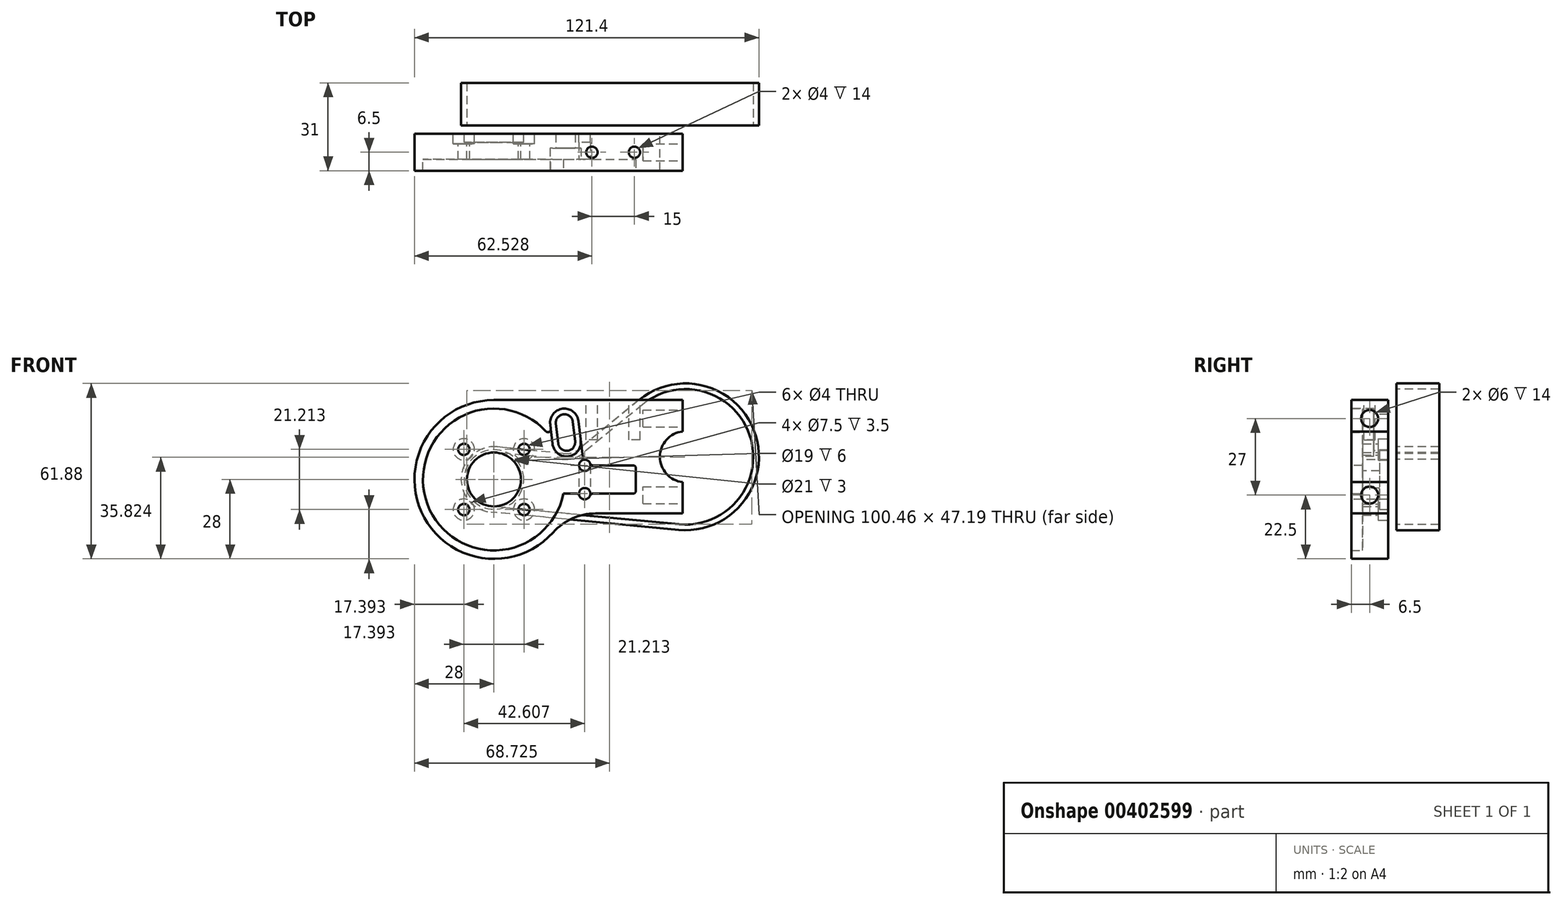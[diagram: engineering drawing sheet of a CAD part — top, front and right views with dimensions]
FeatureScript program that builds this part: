
annotation { "Feature Type Name" : "Feature", "Feature Type Description" : "" }
export const myFeature = defineFeature(function(context is Context, id is Id, definition is map)
    precondition{}
    {
        {
            var Q0;
            Q0=qCreatedBy(makeId("Front.planeOp"),FACE);
            var sketch = newSketch(context, id + "F0", { "sketchPlane" : qUnion([Q0])});
            skArc(sketch, "E0", {"start": v(66.53, 16.94) * mm, "mid": v(58.53, 8) * mm, "end": v(66.53, -0.94) * mm});
            skLineSegment(sketch, "E1", {"start": v(66.53, 16.94) * mm, "end": v(66.53, 28) * mm});
            skLineSegment(sketch, "E2", {"start": v(66.53, -0.94) * mm, "end": v(66.53, -12) * mm});
            skLineSegment(sketch, "E3", {"start": v(66.53, 16.94) * mm, "end": v(66.53, 8) * mm, "construction": true});
            skLineSegment(sketch, "E4", {"start": v(66.53, 8) * mm, "end": v(66.53, -0.94) * mm, "construction": true});
            skArc(sketch, "E5", {"start": v(0, 28) * mm, "mid": v(-25.56, -11.43) * mm, "end": v(20.87, -18.67) * mm});
            skCircle(sketch, "E6", {"center": v(0, 0) * mm, "radius": 11 * mm, "construction": true});
            skLineSegment(sketch, "E7", {"start": v(0, 0) * mm, "end": v(10.6, 10.6) * mm, "construction": true});
            skLineSegment(sketch, "E8", {"start": v(0, 0) * mm, "end": v(-10.6, -10.6) * mm, "construction": true});
            skLineSegment(sketch, "E9", {"start": v(0, 0) * mm, "end": v(10.6, -10.6) * mm, "construction": true});
            skLineSegment(sketch, "E10", {"start": v(0, 0) * mm, "end": v(-10.6, 10.6) * mm, "construction": true});
            skCircle(sketch, "E11", {"center": v(10.6, -10.6) * mm, "radius": 2 * mm});
            skCircle(sketch, "E12", {"center": v(-10.6, -10.6) * mm, "radius": 2 * mm});
            skCircle(sketch, "E13", {"center": v(-10.6, 10.6) * mm, "radius": 2 * mm});
            skCircle(sketch, "E14", {"center": v(10.6, 10.6) * mm, "radius": 2 * mm});
            skLineSegment(sketch, "E15", {"start": v(66.53, 28) * mm, "end": v(0, 28) * mm});
            skLineSegment(sketch, "E16", {"start": v(66.53, -12) * mm, "end": v(35.78, -12) * mm});
            skPoint(sketch, "E17.visualSharp", {"position": v(25.3, -12) * mm});
            skArc(sketch, "E17.filletArc", {"start": v(35.78, -12) * mm, "mid": v(27.61, -13.74) * mm, "end": v(20.87, -18.67) * mm});
            skPoint(sketch, "E18.visualSharp", {"position": v(0, 28) * mm});
            skCircle(sketch, "E19", {"center": v(0, 0) * mm, "radius": 9.55 * mm, "construction": true});
            skLineSegment(sketch, "E20.trimOffspring", {"start": v(58.53, 8) * mm, "end": v(67.53, 8) * mm, "construction": true});
            skPoint(sketch, "E21.trimOffspring.start.orphan", {"position": v(44, -40.8) * mm});
            skLineSegment(sketch, "E22", {"start": v(0, 0) * mm, "end": v(0, 8) * mm, "construction": true});
            skLineSegment(sketch, "E23", {"start": v(0, 8) * mm, "end": v(58.53, 8) * mm, "construction": true});
            skPoint(sketch, "E24.0.midPoint", {"position": v(25.1, 23.83) * mm});
            skCircle(sketch, "E25", {"center": v(0, 0) * mm, "radius": 9 * mm});
            skArc(sketch, "E26", {"start": v(0, 28) * mm, "mid": v(25.56, 11.43) * mm, "end": v(20.87, -18.67) * mm, "construction": true});
            skCircle(sketch, "E27", {"center": v(0, 0) * mm, "radius": 22 * mm, "construction": true});
            skCircle(sketch, "E28", {"center": v(0, 0) * mm, "radius": 25 * mm, "construction": true});
            skCircle(sketch, "E29", {"center": v(67.53, 8) * mm, "radius": 28.65 * mm, "construction": true});
            skCircle(sketch, "E30", {"center": v(67.53, 8) * mm, "radius": 23.88 * mm, "construction": true});
            skPoint(sketch, "E31.orphan", {"position": v(24.2, 21.89) * mm});
            skPoint(sketch, "E24.1.start.orphan", {"position": v(26, 25.77) * mm});
            skPoint(sketch, "E32.start.orphan", {"position": v(29.02, 8) * mm});
            skSolve(sketch);
        }
        {
            var Q0;
            Q0=makeQuery(id+"F0.imprint","IMPRINT",FACE,{"disambiguationData":[TD([[makeQuery(id+"F0.imprint","IMPRINT",EDGE,{"derivedFrom":sQuery(id+"F0.wireOp",EDGE,"E0")}),-1.0]])]});
            extrude(context, id + "F1", {"entities" : qUnion([Q0]), "depth" : 9 * mm});
        }
        {
            var Q0;
            Q0=makeQuery(id+"F1.opExtrude","CAP_FACE",FACE,{"disambiguationData":[OSD([sQuery(id+"F0.wireOp",EDGE,"E0"),sQuery(id+"F0.wireOp",EDGE,"E1"),sQuery(id+"F0.wireOp",EDGE,"E2"),sQuery(id+"F0.wireOp",EDGE,"E5"),sQuery(id+"F0.wireOp",EDGE,"E11"),sQuery(id+"F0.wireOp",EDGE,"E12"),sQuery(id+"F0.wireOp",EDGE,"E13"),sQuery(id+"F0.wireOp",EDGE,"E14"),sQuery(id+"F0.wireOp",EDGE,"E15"),sQuery(id+"F0.wireOp",EDGE,"E16"),sQuery(id+"F0.wireOp",EDGE,"E17.filletArc"),sQuery(id+"F0.wireOp",EDGE,"E25")])],"isStart":true});
            var sketch = newSketch(context, id + "F2", { "sketchPlane" : qUnion([Q0])});
            skCircle(sketch, "E33", {"center": v(0, 0) * mm, "radius": 9.5 * mm});
            skSolve(sketch);
        }
        {
            var Q0;
            Q0 = qSketchRegion(id + "F2", true);
            extrude(context, id + "F3", {"entities" : qUnion([Q0]), "operationType" : NewBodyOperationType.REMOVE, "oppositeDirection" : true, "depth" : 9 * mm});
        }
        {
            var Q0;
            Q0=makeQuery(id+"F1.opExtrude","CAP_FACE",FACE,{"disambiguationData":[OSD([sQuery(id+"F0.wireOp",EDGE,"E0"),sQuery(id+"F0.wireOp",EDGE,"E1"),sQuery(id+"F0.wireOp",EDGE,"E2"),sQuery(id+"F0.wireOp",EDGE,"E5"),sQuery(id+"F0.wireOp",EDGE,"E11"),sQuery(id+"F0.wireOp",EDGE,"E12"),sQuery(id+"F0.wireOp",EDGE,"E13"),sQuery(id+"F0.wireOp",EDGE,"E14"),sQuery(id+"F0.wireOp",EDGE,"E15"),sQuery(id+"F0.wireOp",EDGE,"E16"),sQuery(id+"F0.wireOp",EDGE,"E17.filletArc"),sQuery(id+"F0.wireOp",EDGE,"E25")])],"isStart":false});
            var sketch = newSketch(context, id + "F4", { "sketchPlane" : qUnion([Q0])});
            skArc(sketch, "E34.0", {"start": v(0, 28) * mm, "mid": v(-25.56, -11.43) * mm, "end": v(20.87, -18.67) * mm});
            skLineSegment(sketch, "E35.0", {"start": v(66.53, -12) * mm, "end": v(35.78, -12) * mm});
            skArc(sketch, "E36.0", {"start": v(35.78, -12) * mm, "mid": v(27.61, -13.74) * mm, "end": v(20.87, -18.67) * mm});
            skLineSegment(sketch, "E37.0", {"start": v(66.53, 28) * mm, "end": v(0, 28) * mm});
            skLineSegment(sketch, "E38.0", {"start": v(66.53, -0.94) * mm, "end": v(66.53, -12) * mm});
            skArc(sketch, "E39.0", {"start": v(66.53, 16.94) * mm, "mid": v(58.53, 8) * mm, "end": v(66.53, -0.94) * mm});
            skLineSegment(sketch, "E40.0", {"start": v(66.53, 16.94) * mm, "end": v(66.53, 28) * mm});
            skCircle(sketch, "E41", {"center": v(0, 0) * mm, "radius": 25 * mm});
            skSolve(sketch);
        }
        {
            var Q0;
            Q0 = qSketchRegion(id + "F4", true);
            extrude(context, id + "F5", {"entities" : qUnion([Q0]), "operationType" : NewBodyOperationType.ADD, "depth" : 4 * mm});
        }
        {
            var Q0;
            Q0 = qSketchRegion(id + "F0", true);
            var sketch = newSketch(context, id + "F6", { "sketchPlane" : qUnion([Q0])});
            skLineSegment(sketch, "E42", {"start": v(0, 0) * mm, "end": v(67.53, 8) * mm, "construction": true});
            skLineSegment(sketch, "E43", {"start": v(26.81, 3.18) * mm, "end": v(25.64, 13.1) * mm, "construction": true});
            skLineSegment(sketch, "E44", {"start": v(25.64, 13.1) * mm, "end": v(24.82, 20) * mm, "construction": true});
            skArc(sketch, "E45.0.startCap", {"start": v(30.6, 13.7) * mm, "mid": v(26.22, 8.14) * mm, "end": v(20.67, 12.52) * mm});
            skArc(sketch, "E45.0.endCap", {"start": v(19.85, 19.41) * mm, "mid": v(24.23, 24.97) * mm, "end": v(29.78, 20.59) * mm});
            skLineSegment(sketch, "E45.0.left", {"start": v(20.67, 12.52) * mm, "end": v(19.85, 19.41) * mm});
            skLineSegment(sketch, "E45.0.right", {"start": v(30.6, 13.7) * mm, "end": v(29.78, 20.59) * mm});
            skArc(sketch, "E46.0.startCap", {"start": v(33.58, 14.05) * mm, "mid": v(26.58, 5.16) * mm, "end": v(17.7, 12.17) * mm, "construction": true});
            skArc(sketch, "E46.0.endCap", {"start": v(16.87, 19.06) * mm, "mid": v(23.88, 27.94) * mm, "end": v(32.76, 20.94) * mm, "construction": true});
            skLineSegment(sketch, "E46.0.left", {"start": v(17.7, 12.17) * mm, "end": v(16.87, 19.06) * mm, "construction": true});
            skLineSegment(sketch, "E46.0.right", {"start": v(33.58, 14.05) * mm, "end": v(32.76, 20.94) * mm, "construction": true});
            skSolve(sketch);
        }
        {
            var Q0;
            Q0=makeQuery(id+"F5.opExtrude","CAP_FACE",FACE,{"disambiguationData":[OSD([sQuery(id+"F4.wireOp",EDGE,"E34.0"),sQuery(id+"F4.wireOp",EDGE,"E35.0"),sQuery(id+"F4.wireOp",EDGE,"E36.0"),sQuery(id+"F4.wireOp",EDGE,"E37.0"),sQuery(id+"F4.wireOp",EDGE,"E38.0"),sQuery(id+"F4.wireOp",EDGE,"E39.0"),sQuery(id+"F4.wireOp",EDGE,"E40.0"),sQuery(id+"F4.wireOp",EDGE,"E41")])],"isStart":false});
            var sketch = newSketch(context, id + "F7", { "sketchPlane" : qUnion([Q0])});
            skLineSegment(sketch, "E47.0", {"start": v(30.6, 13.7) * mm, "end": v(29.78, 20.59) * mm});
            skArc(sketch, "E48.0", {"start": v(19.85, 19.41) * mm, "mid": v(24.23, 24.97) * mm, "end": v(29.78, 20.59) * mm});
            skLineSegment(sketch, "E49.0", {"start": v(20.67, 12.52) * mm, "end": v(19.85, 19.41) * mm});
            skLineSegment(sketch, "E50.0", {"start": v(25.64, 13.1) * mm, "end": v(24.82, 20) * mm, "construction": true});
            skArc(sketch, "E51.0", {"start": v(30.6, 13.7) * mm, "mid": v(26.22, 8.14) * mm, "end": v(20.67, 12.52) * mm});
            skPoint(sketch, "E52.0", {"position": v(33.58, 14.05) * mm});
            skLineSegment(sketch, "E53.0", {"start": v(33.58, 14.05) * mm, "end": v(32.76, 20.94) * mm, "construction": true});
            skLineSegment(sketch, "E54.0", {"start": v(0, 0) * mm, "end": v(67.53, 8) * mm, "construction": true});
            skLineSegment(sketch, "E55.0", {"start": v(17.7, 12.17) * mm, "end": v(16.87, 19.06) * mm, "construction": true});
            skArc(sketch, "E56.0", {"start": v(16.87, 19.06) * mm, "mid": v(23.88, 27.94) * mm, "end": v(32.76, 20.94) * mm, "construction": true});
            skArc(sketch, "E57.0", {"start": v(33.58, 14.05) * mm, "mid": v(26.58, 5.16) * mm, "end": v(17.7, 12.17) * mm, "construction": true});
            skSolve(sketch);
        }
        {
            var Q0;
            Q0 = qSketchRegion(id + "F7", true);
            extrude(context, id + "F8", {"entities" : qUnion([Q0]), "operationType" : NewBodyOperationType.REMOVE, "oppositeDirection" : true, "depth" : 8 * mm});
        }
        {
            var Q0;
            Q0=makeQuery(id+"F8.boolean.opBoolean","COPY",FACE,{"derivedFrom":makeQuery(id+"F8.opExtrude","CAP_FACE",FACE,{"disambiguationData":[OSD([sQuery(id+"F7.wireOp",EDGE,"E47.0"),sQuery(id+"F7.wireOp",EDGE,"E48.0"),sQuery(id+"F7.wireOp",EDGE,"E49.0"),sQuery(id+"F7.wireOp",EDGE,"E51.0")])],"isStart":false})});
            var sketch = newSketch(context, id + "F9", { "sketchPlane" : qUnion([Q0])});
            skLineSegment(sketch, "E58", {"start": v(24.82, 20) * mm, "end": v(25.64, 13.1) * mm, "construction": true});
            skArc(sketch, "E59.0.startCap", {"start": v(21.84, 19.65) * mm, "mid": v(24.47, 22.98) * mm, "end": v(27.8, 20.35) * mm});
            skArc(sketch, "E59.0.endCap", {"start": v(28.62, 13.46) * mm, "mid": v(25.99, 10.13) * mm, "end": v(22.66, 12.75) * mm});
            skLineSegment(sketch, "E59.0.left", {"start": v(27.8, 20.35) * mm, "end": v(28.62, 13.46) * mm});
            skLineSegment(sketch, "E59.0.right", {"start": v(21.84, 19.65) * mm, "end": v(22.66, 12.75) * mm});
            skSolve(sketch);
        }
        {
            var Q0;
            Q0 = qSketchRegion(id + "F9", true);
            extrude(context, id + "F10", {"entities" : qUnion([Q0]), "operationType" : NewBodyOperationType.REMOVE, "endBound" : BoundingType.THROUGH_ALL, "oppositeDirection" : true, "depth" : 25 * mm});
        }
        {
            var Q0;
            Q0=makeQuery(id+"F8.boolean.opBoolean","INTERSECT",EDGE,{"derivedFrom":[makeQuery(id+"F5.opExtrude","SWEPT_FACE",FACE,{"disambiguationData":[OSD([sQuery(id+"F4.wireOp",EDGE,"E41")])]}),makeQuery(id+"F8.opExtrude","SWEPT_FACE",FACE,{"disambiguationData":[OSD([sQuery(id+"F7.wireOp",EDGE,"E49.0")])]})]});
            var Q1;
            Q1=makeQuery(id+"F8.boolean.opBoolean","INTERSECT",EDGE,{"derivedFrom":[makeQuery(id+"F5.opExtrude","SWEPT_FACE",FACE,{"disambiguationData":[OSD([sQuery(id+"F4.wireOp",EDGE,"E41")])]}),makeQuery(id+"F8.opExtrude","SWEPT_FACE",FACE,{"disambiguationData":[OSD([sQuery(id+"F7.wireOp",EDGE,"E51.0")])]})]});
            fillet(context, id + "F11", {"entities" : qUnion([Q0, Q1]), "radius" : 1 * mm, "tangentPropagation" : true, "allowEdgeOverflow" : false});
        }
        {
            var Q0;
            {var subQ0=sQuery(id+"F7.wireOp",EDGE,"E47.0");Q0=makeQuery(id+"F7.imprint","IMPRINT",FACE,{"disambiguationData":[TD([[makeQuery(id+"F7.imprint","IMPRINT",EDGE,{"derivedFrom":subQ0}),-1.0]])]});}
            var sketch = newSketch(context, id + "F12", { "sketchPlane" : qUnion([Q0])});
            skLineSegment(sketch, "E60", {"start": v(0, 0) * mm, "end": v(50, 0) * mm, "construction": true});
            skArc(sketch, "E61.0", {"start": v(24.5, -5) * mm, "mid": v(24.98, 0.96) * mm, "end": v(24.04, 6.87) * mm});
            skPoint(sketch, "E62.0", {"position": v(25.1, 8.14) * mm});
            skArc(sketch, "E63.0", {"start": v(30.6, 13.7) * mm, "mid": v(29.2, 9.6) * mm, "end": v(25.1, 8.14) * mm});
            skArc(sketch, "E64.0", {"start": v(25.1, 8.14) * mm, "mid": v(24.23, 7.78) * mm, "end": v(24.04, 6.87) * mm});
            skPoint(sketch, "E65.orphan", {"position": v(20.67, 12.52) * mm});
            skLineSegment(sketch, "E66", {"start": v(50, 0) * mm, "end": v(50, 5) * mm});
            skPoint(sketch, "E67.orphan", {"position": v(30.6, 13.7) * mm});
            skLineSegment(sketch, "E68", {"start": v(50, 0) * mm, "end": v(50, -5) * mm});
            skLineSegment(sketch, "E69", {"start": v(50, -5) * mm, "end": v(24.5, -5) * mm});
            skPoint(sketch, "E70.endSnap0", {"position": v(24.01, 8.38) * mm});
            skLineSegment(sketch, "E71", {"start": v(30.6, 13.7) * mm, "end": v(31.63, 5) * mm});
            skPoint(sketch, "E72.orphan", {"position": v(24.01, 7) * mm});
            skPoint(sketch, "E73.orphan", {"position": v(18.32, 17.01) * mm});
            skLineSegment(sketch, "E74", {"start": v(50, 5) * mm, "end": v(31.63, 5) * mm});
            skSolve(sketch);
        }
        {
            var Q0;
            Q0 = qSketchRegion(id + "F12", true);
            var Q1;
            Q1=makeQuery(id+"F1.opExtrude","CAP_FACE",FACE,{"disambiguationData":[OSD([sQuery(id+"F0.wireOp",EDGE,"E0"),sQuery(id+"F0.wireOp",EDGE,"E1"),sQuery(id+"F0.wireOp",EDGE,"E2"),sQuery(id+"F0.wireOp",EDGE,"E5"),sQuery(id+"F0.wireOp",EDGE,"E11"),sQuery(id+"F0.wireOp",EDGE,"E12"),sQuery(id+"F0.wireOp",EDGE,"E13"),sQuery(id+"F0.wireOp",EDGE,"E14"),sQuery(id+"F0.wireOp",EDGE,"E15"),sQuery(id+"F0.wireOp",EDGE,"E16"),sQuery(id+"F0.wireOp",EDGE,"E17.filletArc"),sQuery(id+"F0.wireOp",EDGE,"E25")])],"isStart":false});
            extrude(context, id + "F13", {"entities" : qUnion([Q0]), "operationType" : NewBodyOperationType.REMOVE, "endBound" : BoundingType.UP_TO_SURFACE, "oppositeDirection" : true, "endBoundEntityFace" : qUnion([Q1]), "depth" : 25 * mm});
        }
        {
            var Q0;
            Q0=makeQuery(id+"F13.boolean.opBoolean","COPY",EDGE,{"derivedFrom":makeQuery(id+"F13.opExtrude","SWEPT_EDGE",EDGE,{"disambiguationData":[OSD([sQuery(id+"F12.wireOp",EDGE,"E70"),sQuery(id+"F12.wireOp",EDGE,"E71")])]})});
            var Q1;
            Q1=makeQuery(id+"F13.boolean.opBoolean","COPY",EDGE,{"derivedFrom":makeQuery(id+"F13.opExtrude","SWEPT_EDGE",EDGE,{"disambiguationData":[OSD([sQuery(id+"F4.wireOp",EDGE,"E41"),sQuery(id+"F12.wireOp",EDGE,"E61.0"),sQuery(id+"F12.wireOp",EDGE,"E69")])]})});
            var Q2;
            Q2=makeQuery(id+"F13.boolean.opBoolean","COPY",EDGE,{"derivedFrom":makeQuery(id+"F13.opExtrude","SWEPT_EDGE",EDGE,{"disambiguationData":[OSD([sQuery(id+"F12.wireOp",EDGE,"E66"),sQuery(id+"F12.wireOp",EDGE,"E70")])]})});
            var Q3;
            Q3=makeQuery(id+"F13.boolean.opBoolean","COPY",EDGE,{"derivedFrom":makeQuery(id+"F13.opExtrude","SWEPT_EDGE",EDGE,{"disambiguationData":[OSD([sQuery(id+"F12.wireOp",EDGE,"E68"),sQuery(id+"F12.wireOp",EDGE,"E69")])]})});
            fillet(context, id + "F14", {"entities" : qUnion([Q0, Q1, Q2, Q3]), "radius" : 1 * mm, "tangentPropagation" : true, "allowEdgeOverflow" : false});
        }
        {
            var Q0;
            Q0=makeQuery(id+"F1.opExtrude","CAP_FACE",FACE,{"disambiguationData":[OSD([sQuery(id+"F0.wireOp",EDGE,"E0"),sQuery(id+"F0.wireOp",EDGE,"E1"),sQuery(id+"F0.wireOp",EDGE,"E2"),sQuery(id+"F0.wireOp",EDGE,"E5"),sQuery(id+"F0.wireOp",EDGE,"E11"),sQuery(id+"F0.wireOp",EDGE,"E12"),sQuery(id+"F0.wireOp",EDGE,"E13"),sQuery(id+"F0.wireOp",EDGE,"E14"),sQuery(id+"F0.wireOp",EDGE,"E15"),sQuery(id+"F0.wireOp",EDGE,"E16"),sQuery(id+"F0.wireOp",EDGE,"E17.filletArc"),sQuery(id+"F0.wireOp",EDGE,"E25")])],"isStart":true});
            var sketch = newSketch(context, id + "F15", { "sketchPlane" : qUnion([Q0])});
            skLineSegment(sketch, "E75", {"start": v(-24.82, 20) * mm, "end": v(-25.64, 13.1) * mm, "construction": true});
            skArc(sketch, "E76", {"start": v(-30.87, 10.12) * mm, "mid": v(-27.76, 8.46) * mm, "end": v(-24.25, 8.13) * mm});
            skArc(sketch, "E77", {"start": v(-51.76, 27.24) * mm, "mid": v(-91.32, 15.26) * mm, "end": v(-65.18, -16.76) * mm});
            skArc(sketch, "E78", {"start": v(1, -10.5) * mm, "mid": v(10.5, 1.03) * mm, "end": v(-1.07, 10.5) * mm});
            skLineSegment(sketch, "E79", {"start": v(-51.76, 27.24) * mm, "end": v(-30.87, 10.12) * mm});
            skLineSegment(sketch, "E80", {"start": v(-65.18, -16.76) * mm, "end": v(1, -10.5) * mm});
            skLineSegment(sketch, "E81", {"start": v(-24.25, 8.13) * mm, "end": v(-1.07, 10.5) * mm});
            skSolve(sketch);
        }
        {
            var Q0;
            Q0=makeQuery(id+"F5.opExtrude","CAP_FACE",FACE,{"disambiguationData":[OSD([sQuery(id+"F4.wireOp",EDGE,"E34.0"),sQuery(id+"F4.wireOp",EDGE,"E35.0"),sQuery(id+"F4.wireOp",EDGE,"E36.0"),sQuery(id+"F4.wireOp",EDGE,"E37.0"),sQuery(id+"F4.wireOp",EDGE,"E38.0"),sQuery(id+"F4.wireOp",EDGE,"E39.0"),sQuery(id+"F4.wireOp",EDGE,"E40.0"),sQuery(id+"F4.wireOp",EDGE,"E41")])],"isStart":false});
            var sketch = newSketch(context, id + "F16", { "sketchPlane" : qUnion([Q0])});
            skCircle(sketch, "E82", {"center": v(32, 5) * mm, "radius": 2 * mm});
            skCircle(sketch, "E83", {"center": v(32, -5) * mm, "radius": 2 * mm});
            skLineSegment(sketch, "E84", {"start": v(32, 5) * mm, "end": v(32, -5) * mm, "construction": true});
            skSolve(sketch);
        }
        {
            var Q0;
            Q0 = qSketchRegion(id + "F16", true);
            extrude(context, id + "F17", {"entities" : qUnion([Q0]), "operationType" : NewBodyOperationType.REMOVE, "endBound" : BoundingType.THROUGH_ALL, "oppositeDirection" : true, "depth" : 25 * mm});
        }
        {
            var Q0;
            Q0=makeQuery(id+"F17.boolean.opBoolean","INTERSECT",EDGE,{"disambiguationData":[OD(1.0)],"derivedFrom":[makeQuery(id+"F13.boolean.opBoolean","COPY",FACE,{"derivedFrom":makeQuery(id+"F13.opExtrude","SWEPT_FACE",FACE,{"disambiguationData":[OSD([sQuery(id+"F12.wireOp",EDGE,"E69")])]})}),makeQuery(id+"F17.opExtrude","SWEPT_FACE",FACE,{"disambiguationData":[OSD([sQuery(id+"F16.wireOp",EDGE,"E83")])]})]});
            var Q1;
            Q1=makeQuery(id+"F17.boolean.opBoolean","INTERSECT",EDGE,{"disambiguationData":[OD(0.0)],"derivedFrom":[makeQuery(id+"F13.boolean.opBoolean","COPY",FACE,{"derivedFrom":makeQuery(id+"F13.opExtrude","SWEPT_FACE",FACE,{"disambiguationData":[OSD([sQuery(id+"F12.wireOp",EDGE,"E69")])]})}),makeQuery(id+"F17.opExtrude","SWEPT_FACE",FACE,{"disambiguationData":[OSD([sQuery(id+"F16.wireOp",EDGE,"E83")])]})]});
            var Q2;
            Q2=makeQuery(id+"F17.boolean.opBoolean","INTERSECT",EDGE,{"disambiguationData":[OD(0.0)],"derivedFrom":[makeQuery(id+"F13.boolean.opBoolean","COPY",FACE,{"derivedFrom":makeQuery(id+"F13.opExtrude","SWEPT_FACE",FACE,{"disambiguationData":[OSD([sQuery(id+"F12.wireOp",EDGE,"E74")])]})}),makeQuery(id+"F17.opExtrude","SWEPT_FACE",FACE,{"disambiguationData":[OSD([sQuery(id+"F16.wireOp",EDGE,"E82")])]})]});
            var Q3;
            Q3=makeQuery(id+"F17.boolean.opBoolean","INTERSECT",EDGE,{"disambiguationData":[OD(1.0)],"derivedFrom":[makeQuery(id+"F13.boolean.opBoolean","COPY",FACE,{"derivedFrom":makeQuery(id+"F13.opExtrude","SWEPT_FACE",FACE,{"disambiguationData":[OSD([sQuery(id+"F12.wireOp",EDGE,"E74")])]})}),makeQuery(id+"F17.opExtrude","SWEPT_FACE",FACE,{"disambiguationData":[OSD([sQuery(id+"F16.wireOp",EDGE,"E82")])]})]});
            var Q4;
            Q4=makeQuery(id+"F17.boolean.opBoolean","INTERSECT",EDGE,{"derivedFrom":[makeQuery(id+"F13.boolean.opBoolean","MERGE",FACE,{"derivedFrom":[makeQuery(id+"F8.boolean.opBoolean","COPY",FACE,{"derivedFrom":makeQuery(id+"F8.opExtrude","SWEPT_FACE",FACE,{"disambiguationData":[OSD([sQuery(id+"F7.wireOp",EDGE,"E47.0")])]})}),makeQuery(id+"F13.opExtrude","SWEPT_FACE",FACE,{"disambiguationData":[OSD([sQuery(id+"F12.wireOp",EDGE,"E71")])]})]}),makeQuery(id+"F17.opExtrude","SWEPT_FACE",FACE,{"disambiguationData":[OSD([sQuery(id+"F16.wireOp",EDGE,"E82")])]})]});
            fillet(context, id + "F18", {"entities" : qUnion([Q0, Q1, Q2, Q3, Q4]), "radius" : 1 * mm, "tangentPropagation" : true, "allowEdgeOverflow" : false});
        }
        {
            var Q0;
            {var subQ2=sQuery(id+"F15.wireOp",EDGE,"E76");Q0=makeQuery(id+"F15.imprint","IMPRINT",FACE,{"disambiguationData":[TD([[makeQuery(id+"F15.imprint","IMPRINT",EDGE,{"derivedFrom":subQ2}),1.0]])]});}
            var sketch = newSketch(context, id + "F19", { "sketchPlane" : qUnion([Q0])});
            skLineSegment(sketch, "E85", {"start": v(-32, 5) * mm, "end": v(-32, -5) * mm, "construction": true});
            skArc(sketch, "E86.0.startCap", {"start": v(-34, 5) * mm, "mid": v(-32, 7) * mm, "end": v(-30, 5) * mm});
            skArc(sketch, "E86.0.endCap", {"start": v(-30, -5) * mm, "mid": v(-32, -7) * mm, "end": v(-34, -5) * mm});
            skLineSegment(sketch, "E86.0.left", {"start": v(-30, 5) * mm, "end": v(-30, -5) * mm});
            skLineSegment(sketch, "E86.0.right", {"start": v(-34, 5) * mm, "end": v(-34, -5) * mm});
            skSolve(sketch);
        }
        {
            var Q0;
            Q0 = qSketchRegion(id + "F19", true);
            extrude(context, id + "F20", {"entities" : qUnion([Q0]), "operationType" : NewBodyOperationType.REMOVE, "oppositeDirection" : true, "depth" : 3 * mm});
        }
        {
            var Q0;
            Q0=makeQuery(id+"F5.boolean.opBoolean","MERGE",FACE,{"derivedFrom":[makeQuery(id+"F1.opExtrude","SWEPT_FACE",FACE,{"disambiguationData":[OSD([sQuery(id+"F0.wireOp",EDGE,"E1")])]}),makeQuery(id+"F5.opExtrude","SWEPT_FACE",FACE,{"disambiguationData":[OSD([sQuery(id+"F4.wireOp",EDGE,"E40.0")])]})]});
            var sketch = newSketch(context, id + "F21", { "sketchPlane" : qUnion([Q0])});
            skLineSegment(sketch, "E87", {"start": v(0, 21.5) * mm, "end": v(-13, 21.5) * mm, "construction": true});
            skCircle(sketch, "E88", {"center": v(-6.5, 21.5) * mm, "radius": 3 * mm});
            skLineSegment(sketch, "E89", {"start": v(0, -5.5) * mm, "end": v(-13, -5.5) * mm, "construction": true});
            skCircle(sketch, "E90", {"center": v(-6.5, -5.5) * mm, "radius": 3 * mm});
            skSolve(sketch);
        }
        {
            var Q0;
            Q0 = qSketchRegion(id + "F21", true);
            extrude(context, id + "F22", {"entities" : qUnion([Q0]), "operationType" : NewBodyOperationType.REMOVE, "oppositeDirection" : true, "depth" : 14 * mm});
        }
        {
            var Q0;
            Q0=makeQuery(id+"F1.opExtrude","CAP_FACE",FACE,{"disambiguationData":[OSD([sQuery(id+"F0.wireOp",EDGE,"E0"),sQuery(id+"F0.wireOp",EDGE,"E1"),sQuery(id+"F0.wireOp",EDGE,"E2"),sQuery(id+"F0.wireOp",EDGE,"E5"),sQuery(id+"F0.wireOp",EDGE,"E11"),sQuery(id+"F0.wireOp",EDGE,"E12"),sQuery(id+"F0.wireOp",EDGE,"E13"),sQuery(id+"F0.wireOp",EDGE,"E14"),sQuery(id+"F0.wireOp",EDGE,"E15"),sQuery(id+"F0.wireOp",EDGE,"E16"),sQuery(id+"F0.wireOp",EDGE,"E17.filletArc"),sQuery(id+"F0.wireOp",EDGE,"E25")])],"isStart":true});
            cPlane(context, id + "F23", {"entities" : qUnion([Q0]), "cplaneType" : CPlaneType.OFFSET, "offset" : 3 * mm, "width" : 150 * mm, "height" : 150 * mm});
        }
        {
            var Q0;
            Q0=qCreatedBy(id+"F23.planeOp",FACE);
            var sketch = newSketch(context, id + "F24", { "sketchPlane" : qUnion([Q0])});
            skArc(sketch, "E91.0", {"start": v(-51.13, 28.01) * mm, "mid": v(-92.28, 15.55) * mm, "end": v(-65.1, -17.76) * mm});
            skArc(sketch, "E91.1", {"start": v(1.09, -11.5) * mm, "mid": v(11.5, 1.13) * mm, "end": v(-1.17, 11.5) * mm});
            skLineSegment(sketch, "E91.2", {"start": v(-24.35, 9.12) * mm, "end": v(-1.17, 11.5) * mm});
            skLineSegment(sketch, "E91.3", {"start": v(-65.1, -17.76) * mm, "end": v(1.09, -11.5) * mm});
            skArc(sketch, "E91.4", {"start": v(-30.24, 10.9) * mm, "mid": v(-27.47, 9.42) * mm, "end": v(-24.35, 9.12) * mm});
            skLineSegment(sketch, "E91.5", {"start": v(-51.13, 28.01) * mm, "end": v(-30.24, 10.9) * mm});
            skArc(sketch, "E92.0", {"start": v(-52.4, 26.47) * mm, "mid": v(-90.36, 14.97) * mm, "end": v(-65.28, -15.77) * mm});
            skArc(sketch, "E92.1", {"start": v(0.9, -9.5) * mm, "mid": v(9.5, 0.94) * mm, "end": v(-0.97, 9.5) * mm});
            skLineSegment(sketch, "E92.2", {"start": v(-24.15, 7.13) * mm, "end": v(-0.97, 9.5) * mm});
            skLineSegment(sketch, "E92.3", {"start": v(-65.28, -15.77) * mm, "end": v(0.9, -9.5) * mm});
            skArc(sketch, "E92.4", {"start": v(-31.5, 9.34) * mm, "mid": v(-28.05, 7.5) * mm, "end": v(-24.15, 7.13) * mm});
            skLineSegment(sketch, "E92.5", {"start": v(-52.4, 26.47) * mm, "end": v(-31.5, 9.34) * mm});
            skSolve(sketch);
        }
        {
            var Q0;
            Q0 = qSketchRegion(id + "F24", true);
            extrude(context, id + "F25", {"entities" : qUnion([Q0]), "depth" : 15 * mm});
        }
        {
            var Q0;
            Q0=makeQuery(id+"F5.boolean.opBoolean","MERGE",FACE,{"derivedFrom":[makeQuery(id+"F1.opExtrude","SWEPT_FACE",FACE,{"disambiguationData":[OSD([sQuery(id+"F0.wireOp",EDGE,"E15")])]}),makeQuery(id+"F5.opExtrude","SWEPT_FACE",FACE,{"disambiguationData":[OSD([sQuery(id+"F4.wireOp",EDGE,"E37.0")])]})]});
            var sketch = newSketch(context, id + "F26", { "sketchPlane" : qUnion([Q0])});
            skLineSegment(sketch, "E93", {"start": v(66.53, -6.5) * mm, "end": v(0, -6.5) * mm, "construction": true});
            skCircle(sketch, "E94", {"center": v(49.53, -6.5) * mm, "radius": 2 * mm});
            skCircle(sketch, "E95", {"center": v(34.53, -6.5) * mm, "radius": 2 * mm});
            skSolve(sketch);
        }
        {
            var Q0;
            Q0 = qSketchRegion(id + "F26", true);
            extrude(context, id + "F27", {"entities" : qUnion([Q0]), "operationType" : NewBodyOperationType.REMOVE, "oppositeDirection" : true, "depth" : 14 * mm});
        }
        {
            var Q0;
            Q0=makeQuery(id+"F2.imprint","IMPRINT",FACE,{"disambiguationData":[TD([[makeQuery(id+"F2.imprint","IMPRINT",EDGE,{"derivedFrom":sQuery(id+"F2.wireOp",EDGE,"E33")}),-1.0]])]});
            var sketch = newSketch(context, id + "F28", { "sketchPlane" : qUnion([Q0])});
            skCircle(sketch, "E96", {"center": v(-10.6, -10.6) * mm, "radius": 3.75 * mm});
            skCircle(sketch, "E97", {"center": v(10.6, -10.6) * mm, "radius": 3.75 * mm});
            skCircle(sketch, "E98", {"center": v(10.6, 10.6) * mm, "radius": 3.75 * mm});
            skCircle(sketch, "E99", {"center": v(-10.6, 10.6) * mm, "radius": 3.75 * mm});
            skSolve(sketch);
        }
        {
            var Q0;
            Q0 = qSketchRegion(id + "F28", true);
            extrude(context, id + "F29", {"entities" : qUnion([Q0]), "operationType" : NewBodyOperationType.REMOVE, "oppositeDirection" : true, "depth" : 3.5 * mm});
        }
        {
            var Q0;
            Q0=makeQuery(id+"F2.imprint","IMPRINT",FACE,{"disambiguationData":[TD([[makeQuery(id+"F2.imprint","IMPRINT",EDGE,{"derivedFrom":sQuery(id+"F2.wireOp",EDGE,"E33")}),-1.0]])]});
            var sketch = newSketch(context, id + "F30", { "sketchPlane" : qUnion([Q0])});
            skCircle(sketch, "E100", {"center": v(0, 0) * mm, "radius": 10.5 * mm});
            skSolve(sketch);
        }
        {
            var Q0;
            Q0 = qSketchRegion(id + "F30", true);
            extrude(context, id + "F31", {"entities" : qUnion([Q0]), "operationType" : NewBodyOperationType.REMOVE, "oppositeDirection" : true, "depth" : 3 * mm});
        }
    });
